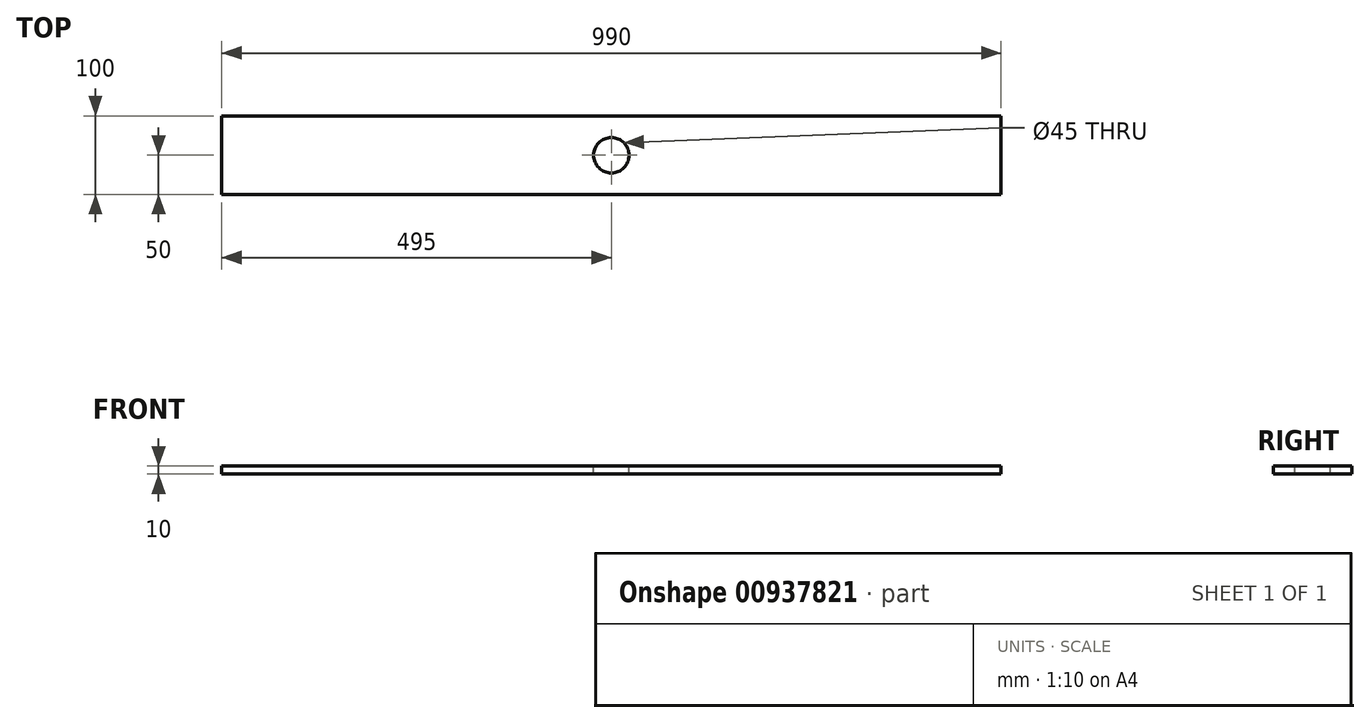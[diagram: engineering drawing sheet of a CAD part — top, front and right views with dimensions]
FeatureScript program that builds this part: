
annotation { "Feature Type Name" : "Feature", "Feature Type Description" : "" }
export const myFeature = defineFeature(function(context is Context, id is Id, definition is map)
    precondition{}
    {
        {
            var Q0;
            Q0=qCreatedBy(makeId("Front.planeOp"),FACE);
            var sketch = newSketch(context, id + "F0", { "sketchPlane" : qUnion([Q0])});
            skLineSegment(sketch, "E0.bottom", {"start": v(495, -5) * mm, "end": v(-495, -5) * mm});
            skLineSegment(sketch, "E0.top", {"start": v(495, 5) * mm, "end": v(-495, 5) * mm});
            skLineSegment(sketch, "E0.left", {"start": v(495, -5) * mm, "end": v(495, 5) * mm});
            skLineSegment(sketch, "E0.right", {"start": v(-495, -5) * mm, "end": v(-495, 5) * mm});
            skPoint(sketch, "E0.middle", {"position": v(0, 0) * mm});
            skSolve(sketch);
        }
        {
            var Q0;
            Q0=makeQuery(id+"F0.imprint","IMPRINT",FACE,{"disambiguationData":[TD([[makeQuery(id+"F0.imprint","IMPRINT",EDGE,{"derivedFrom":sQuery(id+"F0.wireOp",EDGE,"E0.bottom")}),-1.0]])]});
            extrude(context, id + "F1", {"entities" : qUnion([Q0]), "depth" : 100 * mm, "offsetDistance" : 25 * mm});
        }
        {
            var Q0;
            Q0=qCreatedBy(makeId("Top.planeOp"),FACE);
            var sketch = newSketch(context, id + "F2", { "sketchPlane" : qUnion([Q0])});
            skCircle(sketch, "E1", {"center": v(0, -50) * mm, "radius": 22.5 * mm});
            skSolve(sketch);
        }
        {
            var Q0;
            Q0=qSketchRegion(id+"F2",true);
            extrude(context, id + "F3", {"entities" : qUnion([Q0]), "operationType" : NewBodyOperationType.REMOVE, "oppositeDirection" : true, "depth" : 25 * mm, "offsetDistance" : 25 * mm, "symmetric" : true});
        }
    });
